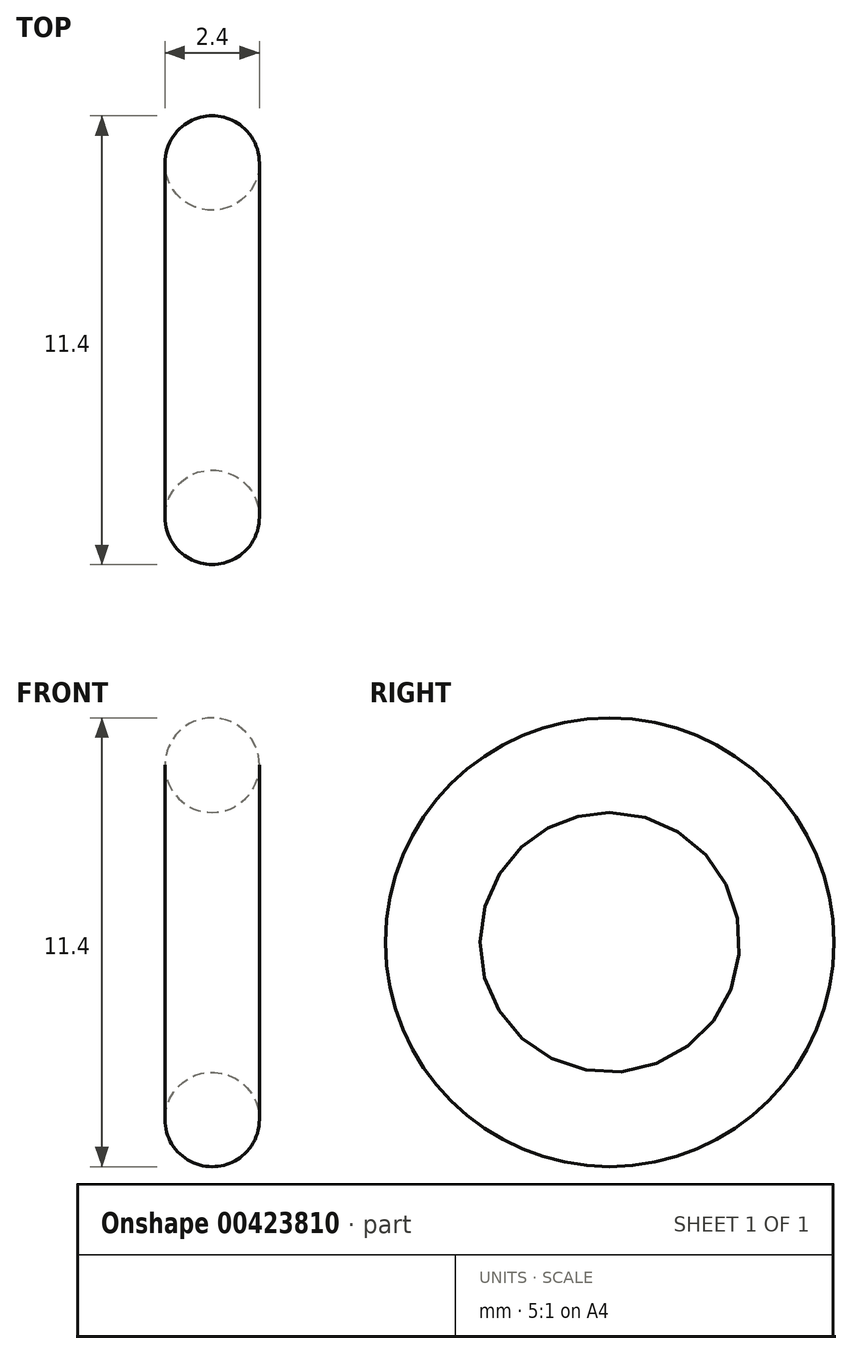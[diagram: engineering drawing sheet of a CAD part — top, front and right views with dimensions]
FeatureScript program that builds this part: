
annotation { "Feature Type Name" : "Feature", "Feature Type Description" : "" }
export const myFeature = defineFeature(function(context is Context, id is Id, definition is map)
    precondition{}
    {
        {
            var Q0;
            Q0=qCreatedBy(makeId("Front.planeOp"),FACE);
            var sketch = newSketch(context, id + "F0", { "sketchPlane" : qUnion([Q0])});
            skCircle(sketch, "E0", {"center": v(0, 4.5) * mm, "radius": 1.2 * mm});
            skPoint(sketch, "E1", {"position": v(0, 0) * mm});
            skLineSegment(sketch, "E2.bottom", {"start": v(-1.2, 5.7) * mm, "end": v(1.2, 5.7) * mm});
            skLineSegment(sketch, "E2.top", {"start": v(-1.2, 0) * mm, "end": v(1.2, 0) * mm});
            skLineSegment(sketch, "E2.left", {"start": v(-1.2, 5.7) * mm, "end": v(-1.2, 0) * mm});
            skLineSegment(sketch, "E2.right", {"start": v(1.2, 5.7) * mm, "end": v(1.2, 0) * mm});
            skSolve(sketch);
        }
        {
            var Q0;
            {var subQ0=sQuery(id+"F0.wireOp",EDGE,"E0");var subQ1=makeQuery(id+"F0.imprint","INTERSECT",VERTEX,{"derivedFrom":[subQ0,sQuery(id+"F0.wireOp",EDGE,"E2.bottom")]});Q0=makeQuery(id+"F0.imprint","IMPRINT",FACE,{"disambiguationData":[TD([[makeQuery(id+"F0.imprint","IMPRINT",EDGE,{"disambiguationData":[TD([[subQ1,1.0]])],"derivedFrom":subQ0}),1.0]])]});}
            var Q1;
            Q1=sQuery(id+"F0.wireOp",EDGE,"E2.top");
            revolve(context, id + "F1", {"entities" : qUnion([Q0]), "axis" : qUnion([Q1]), "revolveType" : RevolveType.FULL});
        }
    });
